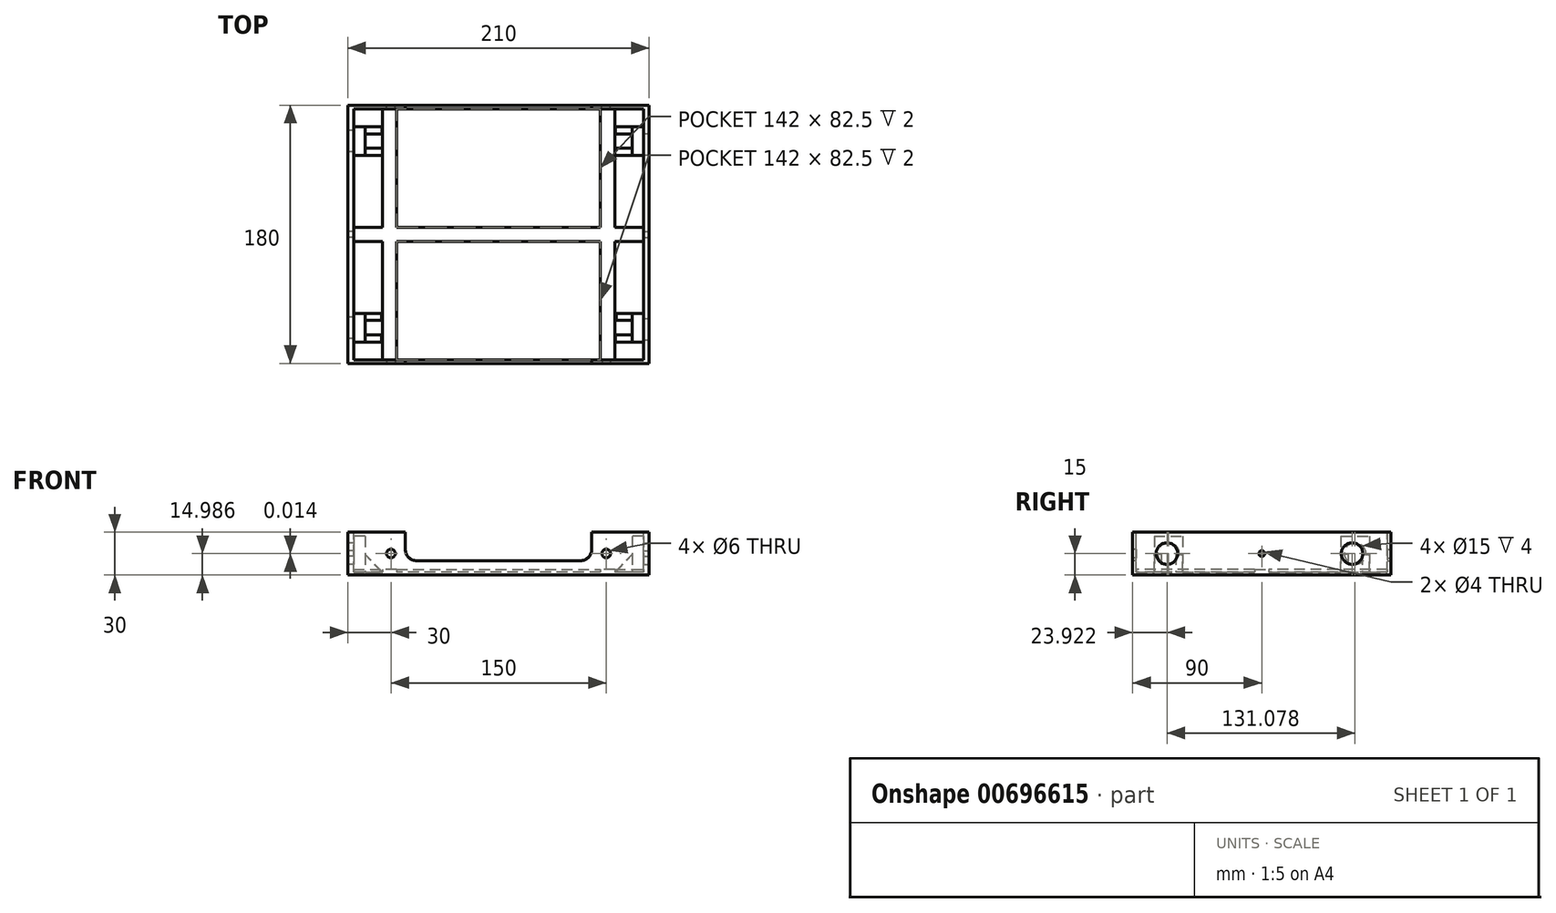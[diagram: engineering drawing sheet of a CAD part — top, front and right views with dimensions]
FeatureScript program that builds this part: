
annotation { "Feature Type Name" : "Feature", "Feature Type Description" : "" }
export const myFeature = defineFeature(function(context is Context, id is Id, definition is map)
    precondition{}
    {
        {
            var Q0;
            Q0=qCreatedBy(makeId("Top.planeOp"),FACE);
            var sketch = newSketch(context, id + "F0", { "sketchPlane" : qUnion([Q0])});
            skLineSegment(sketch, "E0.bottom", {"start": v(105, -90) * mm, "end": v(-105, -90) * mm});
            skLineSegment(sketch, "E0.top", {"start": v(105, 90) * mm, "end": v(-105, 90) * mm});
            skLineSegment(sketch, "E0.left", {"start": v(105, -90) * mm, "end": v(105, 90) * mm});
            skLineSegment(sketch, "E0.right", {"start": v(-105, -90) * mm, "end": v(-105, 90) * mm});
            skPoint(sketch, "E0.middle", {"position": v(0, 0) * mm});
            skSolve(sketch);
        }
        {
            var Q0;
            Q0=makeQuery(id+"F0.imprint","IMPRINT",FACE,{"disambiguationData":[TD([[makeQuery(id+"F0.imprint","IMPRINT",EDGE,{"derivedFrom":sQuery(id+"F0.wireOp",EDGE,"E0.bottom")}),-1.0]])]});
            extrude(context, id + "F1", {"entities" : qUnion([Q0]), "depth" : 30 * mm, "offsetDistance" : 25 * mm});
        }
        {
            var Q0;
            Q0=makeQuery(id+"F1.opExtrude","CAP_FACE",FACE,{"disambiguationData":[OSD([sQuery(id+"F0.wireOp",EDGE,"E0.bottom"),sQuery(id+"F0.wireOp",EDGE,"E0.top"),sQuery(id+"F0.wireOp",EDGE,"E0.left"),sQuery(id+"F0.wireOp",EDGE,"E0.right")])],"isStart":false});
            var sketch = newSketch(context, id + "F2", { "sketchPlane" : qUnion([Q0])});
            skLineSegment(sketch, "E1.bottom", {"start": v(101, -87.5) * mm, "end": v(-101, -87.5) * mm});
            skLineSegment(sketch, "E1.top", {"start": v(101, 87.5) * mm, "end": v(-101, 87.5) * mm});
            skLineSegment(sketch, "E1.left", {"start": v(101, -87.5) * mm, "end": v(101, 87.5) * mm});
            skLineSegment(sketch, "E1.right", {"start": v(-101, -87.5) * mm, "end": v(-101, 87.5) * mm});
            skPoint(sketch, "E1.middle", {"position": v(0, 0) * mm});
            skSolve(sketch);
        }
        {
            var Q0;
            Q0=makeQuery(id+"F2.imprint","IMPRINT",FACE,{"disambiguationData":[TD([[makeQuery(id+"F2.imprint","IMPRINT",EDGE,{"derivedFrom":sQuery(id+"F2.wireOp",EDGE,"E1.bottom")}),-1.0]])]});
            extrude(context, id + "F3", {"entities" : qUnion([Q0]), "operationType" : NewBodyOperationType.REMOVE, "oppositeDirection" : true, "depth" : 28 * mm, "offsetDistance" : 25 * mm});
        }
        {
            var Q0;
            Q0=makeQuery(id+"F1.opExtrude","SWEPT_FACE",FACE,{"disambiguationData":[OSD([sQuery(id+"F0.wireOp",EDGE,"E0.bottom")])]});
            var sketch = newSketch(context, id + "F4", { "sketchPlane" : qUnion([Q0])});
            skLineSegment(sketch, "E2", {"start": v(0, 15) * mm, "end": v(0, 30) * mm, "construction": true});
            skPoint(sketch, "E2.startSnap0", {"position": v(-105, 15) * mm});
            skPoint(sketch, "E2.startSnap1", {"position": v(0, 30) * mm});
            skLineSegment(sketch, "E3", {"start": v(0, 15) * mm, "end": v(-105, 15) * mm, "construction": true});
            skLineSegment(sketch, "E4", {"start": v(0, 15) * mm, "end": v(105, 15) * mm, "construction": true});
            skLineSegment(sketch, "E5", {"start": v(-105, 0) * mm, "end": v(-75, 0) * mm, "construction": true});
            skLineSegment(sketch, "E6", {"start": v(105, 0) * mm, "end": v(75, 0) * mm, "construction": true});
            skLineSegment(sketch, "E7", {"start": v(-75, 0) * mm, "end": v(-75, 30) * mm, "construction": true});
            skLineSegment(sketch, "E8", {"start": v(75, 0) * mm, "end": v(75, 30) * mm, "construction": true});
            skCircle(sketch, "E9", {"center": v(-75, 15) * mm, "radius": 3 * mm});
            skCircle(sketch, "E10", {"center": v(75, 15) * mm, "radius": 3 * mm});
            skLineSegment(sketch, "E11", {"start": v(-105, 30) * mm, "end": v(-65, 30) * mm, "construction": true});
            skLineSegment(sketch, "E12", {"start": v(105, 30) * mm, "end": v(73, 30) * mm, "construction": true});
            skLineSegment(sketch, "E13", {"start": v(-105, 0) * mm, "end": v(-105, 8) * mm, "construction": true});
            skLineSegment(sketch, "E14", {"start": v(-57, 10) * mm, "end": v(57, 10) * mm, "construction": true});
            skLineSegment(sketch, "E15", {"start": v(-15, 30) * mm, "end": v(-15, 0) * mm, "construction": true});
            skLineSegment(sketch, "E16", {"start": v(15, 30) * mm, "end": v(15, 0) * mm, "construction": true});
            skLineSegment(sketch, "E17", {"start": v(-15, 10) * mm, "end": v(-15, 0) * mm});
            skLineSegment(sketch, "E18", {"start": v(15, 10) * mm, "end": v(15, 0) * mm});
            skLineSegment(sketch, "E19", {"start": v(-15, 10) * mm, "end": v(15, 10) * mm});
            skLineSegment(sketch, "E20", {"start": v(-65, 30) * mm, "end": v(-65, 18) * mm, "construction": true});
            skLineSegment(sketch, "E21", {"start": v(65, 22) * mm, "end": v(65, 18) * mm, "construction": true});
            skLineSegment(sketch, "E22", {"start": v(65, 30) * mm, "end": v(65, 18) * mm});
            skLineSegment(sketch, "E23", {"start": v(57, 10) * mm, "end": v(15, 10) * mm});
            skLineSegment(sketch, "E24", {"start": v(-65, 30) * mm, "end": v(-65, 18) * mm});
            skLineSegment(sketch, "E25", {"start": v(-57, 10) * mm, "end": v(-15, 10) * mm});
            skPoint(sketch, "E26.newPointA", {"position": v(-65, 0) * mm});
            skArc(sketch, "E26.filletArc", {"start": v(-65, 18) * mm, "mid": v(-62.66, 12.34) * mm, "end": v(-57, 10) * mm, "construction": true});
            skPoint(sketch, "E27.newPointA", {"position": v(65, 0) * mm});
            skArc(sketch, "E27.filletArc", {"start": v(57, 10) * mm, "mid": v(62.66, 12.34) * mm, "end": v(65, 18) * mm, "construction": true});
            skPoint(sketch, "E28.visualSharp", {"position": v(-65, 10) * mm});
            skArc(sketch, "E28.filletArc", {"start": v(-65, 18) * mm, "mid": v(-62.66, 12.34) * mm, "end": v(-57, 10) * mm});
            skPoint(sketch, "E29.visualSharp", {"position": v(65, 10) * mm});
            skArc(sketch, "E29.filletArc", {"start": v(57, 10) * mm, "mid": v(62.66, 12.34) * mm, "end": v(65, 18) * mm});
            skPoint(sketch, "E30.visualSharp", {"position": v(65, 30) * mm});
            skArc(sketch, "E30.filletArc", {"start": v(73, 30) * mm, "mid": v(67.34, 27.66) * mm, "end": v(65, 22) * mm, "construction": true});
            skSolve(sketch);
        }
        {
            var Q0;
            Q0=makeQuery(id+"F4.imprint","IMPRINT",FACE,{"disambiguationData":[TD([[makeQuery(id+"F4.imprint","IMPRINT",EDGE,{"derivedFrom":sQuery(id+"F4.wireOp",EDGE,"E19")}),1.0]])]});
            var Q1;
            Q1=makeQuery(id+"F4.imprint","IMPRINT",FACE,{"disambiguationData":[TD([[makeQuery(id+"F4.imprint","IMPRINT",EDGE,{"derivedFrom":sQuery(id+"F4.wireOp",EDGE,"E9")}),1.0]])]});
            var Q2;
            Q2=makeQuery(id+"F4.imprint","IMPRINT",FACE,{"disambiguationData":[TD([[makeQuery(id+"F4.imprint","IMPRINT",EDGE,{"derivedFrom":sQuery(id+"F4.wireOp",EDGE,"E10")}),1.0]])]});
            extrude(context, id + "F5", {"entities" : qUnion([Q0, Q1, Q2]), "operationType" : NewBodyOperationType.REMOVE, "oppositeDirection" : true, "depth" : 4 * mm, "offsetDistance" : 25 * mm});
        }
        {
            var Q0;
            Q0=makeQuery(id+"F3.boolean.opBoolean","COPY",FACE,{"derivedFrom":makeQuery(id+"F3.opExtrude","CAP_FACE",FACE,{"disambiguationData":[OSD([sQuery(id+"F2.wireOp",EDGE,"E1.bottom"),sQuery(id+"F2.wireOp",EDGE,"E1.top"),sQuery(id+"F2.wireOp",EDGE,"E1.left"),sQuery(id+"F2.wireOp",EDGE,"E1.right")])],"isStart":false})});
            var sketch = newSketch(context, id + "F6", { "sketchPlane" : qUnion([Q0])});
            skLineSegment(sketch, "E31", {"start": v(-101, 87.5) * mm, "end": v(-81, 87.5) * mm, "construction": true});
            skLineSegment(sketch, "E32.bottom", {"start": v(-81, 87.5) * mm, "end": v(-71, 87.5) * mm});
            skLineSegment(sketch, "E32.top", {"start": v(-81, -87.5) * mm, "end": v(-71, -87.5) * mm});
            skLineSegment(sketch, "E32.left", {"start": v(-81, 87.5) * mm, "end": v(-81, -87.5) * mm});
            skLineSegment(sketch, "E32.right", {"start": v(-71, 87.5) * mm, "end": v(-71, -87.5) * mm});
            skLineSegment(sketch, "E33", {"start": v(101, 87.5) * mm, "end": v(81, 87.5) * mm, "construction": true});
            skLineSegment(sketch, "E34.bottom", {"start": v(81, 87.5) * mm, "end": v(71, 87.5) * mm});
            skLineSegment(sketch, "E34.top", {"start": v(81, -87.5) * mm, "end": v(71, -87.5) * mm});
            skLineSegment(sketch, "E34.left", {"start": v(81, 87.5) * mm, "end": v(81, -87.5) * mm});
            skLineSegment(sketch, "E34.right", {"start": v(71, 87.5) * mm, "end": v(71, -87.5) * mm});
            skLineSegment(sketch, "E35.bottom", {"start": v(-101, 5) * mm, "end": v(101, 5) * mm});
            skLineSegment(sketch, "E35.top", {"start": v(-101, -5) * mm, "end": v(101, -5) * mm});
            skLineSegment(sketch, "E35.left", {"start": v(-101, 5) * mm, "end": v(-101, -5) * mm});
            skLineSegment(sketch, "E35.right", {"start": v(101, 5) * mm, "end": v(101, -5) * mm});
            skPoint(sketch, "E35.middle", {"position": v(0, 0) * mm});
            skSolve(sketch);
        }
        {
            var Q0;
            Q0=makeQuery(id+"F6.imprint","IMPRINT",FACE,{"disambiguationData":[TD([[makeQuery(id+"F6.imprint","IMPRINT",EDGE,{"derivedFrom":sQuery(id+"F6.wireOp",EDGE,"E32.bottom")}),1.0]])]});
            var Q1;
            Q1=makeQuery(id+"F6.imprint","IMPRINT",FACE,{"disambiguationData":[TD([[makeQuery(id+"F6.imprint","IMPRINT",EDGE,{"derivedFrom":sQuery(id+"F6.wireOp",EDGE,"E34.bottom")}),1.0]])]});
            var Q2;
            {var subQ5=sQuery(id+"F6.wireOp",EDGE,"E35.left");Q2=makeQuery(id+"F6.imprint","IMPRINT",FACE,{"disambiguationData":[TD([[makeQuery(id+"F6.imprint","IMPRINT",EDGE,{"derivedFrom":subQ5}),-1.0]])]});}
            var Q3;
            {var subQ0=sQuery(id+"F6.wireOp",EDGE,"E35.bottom");var subQ1=sQuery(id+"F6.wireOp",EDGE,"E32.left");var subQ2=makeQuery(id+"F6.imprint","INTERSECT",VERTEX,{"derivedFrom":[subQ1,subQ0]});Q3=makeQuery(id+"F6.imprint","IMPRINT",FACE,{"disambiguationData":[TD([[makeQuery(id+"F6.imprint","IMPRINT",EDGE,{"disambiguationData":[TD([[subQ2,-1.0]])],"derivedFrom":subQ1}),1.0]])]});}
            var Q4;
            {var subQ0=sQuery(id+"F6.wireOp",EDGE,"E32.top");Q4=makeQuery(id+"F6.imprint","IMPRINT",FACE,{"disambiguationData":[TD([[makeQuery(id+"F6.imprint","IMPRINT",EDGE,{"derivedFrom":subQ0}),-1.0]])]});}
            var Q5;
            {var subQ0=sQuery(id+"F6.wireOp",EDGE,"E35.bottom");var subQ1=sQuery(id+"F6.wireOp",EDGE,"E32.right");var subQ2=makeQuery(id+"F6.imprint","INTERSECT",VERTEX,{"derivedFrom":[subQ1,subQ0]});Q5=makeQuery(id+"F6.imprint","IMPRINT",FACE,{"disambiguationData":[TD([[makeQuery(id+"F6.imprint","IMPRINT",EDGE,{"disambiguationData":[TD([[subQ2,-1.0]])],"derivedFrom":subQ1}),1.0]])]});}
            var Q6;
            {var subQ0=sQuery(id+"F6.wireOp",EDGE,"E35.bottom");var subQ1=sQuery(id+"F6.wireOp",EDGE,"E34.left");var subQ2=makeQuery(id+"F6.imprint","INTERSECT",VERTEX,{"derivedFrom":[subQ1,subQ0]});Q6=makeQuery(id+"F6.imprint","IMPRINT",FACE,{"disambiguationData":[TD([[makeQuery(id+"F6.imprint","IMPRINT",EDGE,{"disambiguationData":[TD([[subQ2,-1.0]])],"derivedFrom":subQ1}),-1.0]])]});}
            var Q7;
            {var subQ0=sQuery(id+"F6.wireOp",EDGE,"E34.top");Q7=makeQuery(id+"F6.imprint","IMPRINT",FACE,{"disambiguationData":[TD([[makeQuery(id+"F6.imprint","IMPRINT",EDGE,{"derivedFrom":subQ0}),-1.0]])]});}
            var Q8;
            {var subQ5=sQuery(id+"F6.wireOp",EDGE,"E35.right");Q8=makeQuery(id+"F6.imprint","IMPRINT",FACE,{"disambiguationData":[TD([[makeQuery(id+"F6.imprint","IMPRINT",EDGE,{"derivedFrom":subQ5}),1.0]])]});}
            extrude(context, id + "F7", {"entities" : qUnion([Q0, Q1, Q2, Q3, Q4, Q5, Q6, Q7, Q8]), "depth" : 2 * mm, "offsetDistance" : 25 * mm});
        }
        {
            var Q0;
            Q0=makeQuery(id+"F1.opExtrude","SWEPT_FACE",FACE,{"disambiguationData":[OSD([sQuery(id+"F0.wireOp",EDGE,"E0.left")])]});
            var sketch = newSketch(context, id + "F8", { "sketchPlane" : qUnion([Q0])});
            skLineSegment(sketch, "E36", {"start": v(0, 30) * mm, "end": v(0, 0) * mm, "construction": true});
            skLineSegment(sketch, "E37", {"start": v(-90, 15) * mm, "end": v(90, 15) * mm, "construction": true});
            skCircle(sketch, "E38", {"center": v(0, 15) * mm, "radius": 2 * mm});
            skSolve(sketch);
        }
        {
            var Q0;
            Q0=makeQuery(id+"F8.imprint","IMPRINT",FACE,{"disambiguationData":[TD([[makeQuery(id+"F8.imprint","IMPRINT",EDGE,{"derivedFrom":sQuery(id+"F8.wireOp",EDGE,"E38")}),1.0]])]});
            var Q1;
            Q1=makeQuery(id+"F8.imprint","IMPRINT",FACE,{"disambiguationData":[TD([[makeQuery(id+"F8.imprint","IMPRINT",EDGE,{"derivedFrom":sQuery(id+"F8.wireOp",EDGE,"LcwHPbP9-Mx9n-9gbT-e416-QBVYges8Fovk")}),1.0]])]});
            extrude(context, id + "F9", {"entities" : qUnion([Q0, Q1]), "operationType" : NewBodyOperationType.REMOVE, "oppositeDirection" : true, "depth" : 5 * mm, "offsetDistance" : 25 * mm});
        }
        {
            var Q0;
            Q0=makeQuery(id+"F1.opExtrude","SWEPT_FACE",FACE,{"disambiguationData":[OSD([sQuery(id+"F0.wireOp",EDGE,"E0.right")])]});
            var sketch = newSketch(context, id + "F10", { "sketchPlane" : qUnion([Q0])});
            skLineSegment(sketch, "E39", {"start": v(0, 30) * mm, "end": v(0, 0) * mm, "construction": true});
            skLineSegment(sketch, "E40", {"start": v(-90, 15) * mm, "end": v(90, 15) * mm, "construction": true});
            skCircle(sketch, "E41", {"center": v(0, 15) * mm, "radius": 2 * mm});
            skLineSegment(sketch, "E42", {"start": v(-65, 30) * mm, "end": v(-65, 0) * mm, "construction": true});
            skLineSegment(sketch, "E43", {"start": v(65, 30) * mm, "end": v(65, 0) * mm, "construction": true});
            skCircle(sketch, "E44", {"center": v(-65, 15) * mm, "radius": 7.5 * mm});
            skCircle(sketch, "E45", {"center": v(65, 15) * mm, "radius": 7.5 * mm});
            skSolve(sketch);
        }
        {
            var Q0;
            Q0=makeQuery(id+"F10.imprint","IMPRINT",FACE,{"disambiguationData":[TD([[makeQuery(id+"F10.imprint","IMPRINT",EDGE,{"derivedFrom":sQuery(id+"F10.wireOp",EDGE,"E41")}),1.0]])]});
            var Q1;
            Q1=makeQuery(id+"F10.imprint","IMPRINT",FACE,{"disambiguationData":[TD([[makeQuery(id+"F10.imprint","IMPRINT",EDGE,{"derivedFrom":sQuery(id+"F10.wireOp",EDGE,"E44")}),1.0]])]});
            var Q2;
            Q2=makeQuery(id+"F10.imprint","IMPRINT",FACE,{"disambiguationData":[TD([[makeQuery(id+"F10.imprint","IMPRINT",EDGE,{"derivedFrom":sQuery(id+"F10.wireOp",EDGE,"E45")}),1.0]])]});
            extrude(context, id + "F11", {"entities" : qUnion([Q0, Q1, Q2]), "operationType" : NewBodyOperationType.REMOVE, "oppositeDirection" : true, "depth" : 5 * mm, "offsetDistance" : 25 * mm});
        }
        {
            var Q0;
            Q0=makeQuery(id+"F1.opExtrude","SWEPT_FACE",FACE,{"disambiguationData":[OSD([sQuery(id+"F0.wireOp",EDGE,"E0.left")])]});
            var sketch = newSketch(context, id + "F12", { "sketchPlane" : qUnion([Q0])});
            skLineSegment(sketch, "E46", {"start": v(-66.08, 30) * mm, "end": v(-66.08, 0) * mm, "construction": true});
            skLineSegment(sketch, "E47", {"start": v(62.94, 30) * mm, "end": v(62.94, 0) * mm, "construction": true});
            skLineSegment(sketch, "E48", {"start": v(-90, 15) * mm, "end": v(90, 15) * mm, "construction": true});
            skCircle(sketch, "E49", {"center": v(-66.08, 15) * mm, "radius": 7.5 * mm});
            skCircle(sketch, "E50", {"center": v(62.94, 15) * mm, "radius": 7.5 * mm});
            skSolve(sketch);
        }
        {
            var Q0;
            Q0=makeQuery(id+"F12.imprint","IMPRINT",FACE,{"disambiguationData":[TD([[makeQuery(id+"F12.imprint","IMPRINT",EDGE,{"derivedFrom":sQuery(id+"F12.wireOp",EDGE,"E49")}),1.0]])]});
            var Q1;
            Q1=makeQuery(id+"F12.imprint","IMPRINT",FACE,{"disambiguationData":[TD([[makeQuery(id+"F12.imprint","IMPRINT",EDGE,{"derivedFrom":sQuery(id+"F12.wireOp",EDGE,"E50")}),1.0]])]});
            extrude(context, id + "F13", {"entities" : qUnion([Q0, Q1]), "operationType" : NewBodyOperationType.REMOVE, "oppositeDirection" : true, "depth" : 5 * mm, "offsetDistance" : 25 * mm});
        }
        {
            var Q0;
            Q0=makeQuery(id+"F3.boolean.opBoolean","COPY",FACE,{"derivedFrom":makeQuery(id+"F3.opExtrude","CAP_FACE",FACE,{"disambiguationData":[OSD([sQuery(id+"F2.wireOp",EDGE,"E1.bottom"),sQuery(id+"F2.wireOp",EDGE,"E1.top"),sQuery(id+"F2.wireOp",EDGE,"E1.left"),sQuery(id+"F2.wireOp",EDGE,"E1.right")])],"isStart":false})});
            var sketch = newSketch(context, id + "F14", { "sketchPlane" : qUnion([Q0])});
            skLineSegment(sketch, "E51", {"start": v(-101, 65) * mm, "end": v(101, 65) * mm, "construction": true});
            skLineSegment(sketch, "E52", {"start": v(-101, -65) * mm, "end": v(101, -65) * mm, "construction": true});
            skLineSegment(sketch, "E53", {"start": v(-97, 87.5) * mm, "end": v(-97, -87.5) * mm, "construction": true});
            skLineSegment(sketch, "E54", {"start": v(97, 87.5) * mm, "end": v(97, -87.5) * mm, "construction": true});
            skPoint(sketch, "E55.middle", {"position": v(-97, -65) * mm});
            skLineSegment(sketch, "E56.bottom", {"start": v(-93, -75) * mm, "end": v(-101, -75) * mm});
            skLineSegment(sketch, "E56.top", {"start": v(-93, -55) * mm, "end": v(-101, -55) * mm});
            skLineSegment(sketch, "E56.left", {"start": v(-93, -75) * mm, "end": v(-93, -55) * mm});
            skLineSegment(sketch, "E56.right", {"start": v(-101, -75) * mm, "end": v(-101, -55) * mm});
            skLineSegment(sketch, "E57.bottom", {"start": v(-93, 55) * mm, "end": v(-101, 55) * mm});
            skLineSegment(sketch, "E57.top", {"start": v(-93, 75) * mm, "end": v(-101, 75) * mm});
            skLineSegment(sketch, "E57.left", {"start": v(-93, 55) * mm, "end": v(-93, 75) * mm});
            skLineSegment(sketch, "E57.right", {"start": v(-101, 55) * mm, "end": v(-101, 75) * mm});
            skPoint(sketch, "E57.middle", {"position": v(-97, 65) * mm});
            skLineSegment(sketch, "E58.bottom", {"start": v(101, 55) * mm, "end": v(93, 55) * mm});
            skLineSegment(sketch, "E58.top", {"start": v(101, 75) * mm, "end": v(93, 75) * mm});
            skLineSegment(sketch, "E58.left", {"start": v(101, 55) * mm, "end": v(101, 75) * mm});
            skLineSegment(sketch, "E58.right", {"start": v(93, 55) * mm, "end": v(93, 75) * mm});
            skPoint(sketch, "E58.middle", {"position": v(97, 65) * mm});
            skLineSegment(sketch, "E59.bottom", {"start": v(101, -75) * mm, "end": v(93, -75) * mm});
            skLineSegment(sketch, "E59.top", {"start": v(101, -55) * mm, "end": v(93, -55) * mm});
            skLineSegment(sketch, "E59.left", {"start": v(101, -75) * mm, "end": v(101, -55) * mm});
            skLineSegment(sketch, "E59.right", {"start": v(93, -75) * mm, "end": v(93, -55) * mm});
            skPoint(sketch, "E59.middle", {"position": v(97, -65) * mm});
            skSolve(sketch);
        }
        {
            var Q0;
            Q0=makeQuery(id+"F14.imprint","IMPRINT",FACE,{"disambiguationData":[TD([[makeQuery(id+"F14.imprint","IMPRINT",EDGE,{"derivedFrom":sQuery(id+"F14.wireOp",EDGE,"E57.bottom")}),-1.0]])]});
            var Q1;
            Q1=makeQuery(id+"F14.imprint","IMPRINT",FACE,{"disambiguationData":[TD([[makeQuery(id+"F14.imprint","IMPRINT",EDGE,{"derivedFrom":sQuery(id+"F14.wireOp",EDGE,"E56.bottom")}),-1.0]])]});
            var Q2;
            Q2=makeQuery(id+"F14.imprint","IMPRINT",FACE,{"disambiguationData":[TD([[makeQuery(id+"F14.imprint","IMPRINT",EDGE,{"derivedFrom":sQuery(id+"F14.wireOp",EDGE,"E58.bottom")}),-1.0]])]});
            var Q3;
            Q3=makeQuery(id+"F14.imprint","IMPRINT",FACE,{"disambiguationData":[TD([[makeQuery(id+"F14.imprint","IMPRINT",EDGE,{"derivedFrom":sQuery(id+"F14.wireOp",EDGE,"E59.bottom")}),-1.0]])]});
            extrude(context, id + "F15", {"entities" : qUnion([Q0, Q1, Q2, Q3]), "operationType" : NewBodyOperationType.ADD, "depth" : 25 * mm, "offsetDistance" : 25 * mm});
        }
        {
            var Q0;
            Q0=makeQuery(id+"F15.opExtrude","SWEPT_FACE",FACE,{"disambiguationData":[OSD([sQuery(id+"F14.wireOp",EDGE,"E59.top")])]});
            var sketch = newSketch(context, id + "F16", { "sketchPlane" : qUnion([Q0])});
            skLineSegment(sketch, "E60", {"start": v(-81.63, 1.7) * mm, "end": v(-93, 2) * mm});
            skLineSegment(sketch, "E61", {"start": v(-81.63, 1.7) * mm, "end": v(-93, 14.5) * mm});
            skSolve(sketch);
        }
        {
            var Q0;
            {var subQ0=sQuery(id+"F16.wireOp",EDGE,"E60");Q0=makeQuery(id+"F16.imprint","IMPRINT",FACE,{"disambiguationData":[TD([[makeQuery(id+"F16.imprint","IMPRINT",EDGE,{"derivedFrom":subQ0}),-1.0]])]});}
            extrude(context, id + "F17", {"entities" : qUnion([Q0]), "operationType" : NewBodyOperationType.ADD, "oppositeDirection" : true, "depth" : 5 * mm, "offsetDistance" : 25 * mm});
        }
        {
            var Q0;
            Q0=makeQuery(id+"F15.opExtrude","SWEPT_FACE",FACE,{"disambiguationData":[OSD([sQuery(id+"F14.wireOp",EDGE,"E57.bottom")])]});
            var sketch = newSketch(context, id + "F18", { "sketchPlane" : qUnion([Q0])});
            skLineSegment(sketch, "E62", {"start": v(-93, 2) * mm, "end": v(-81.02, 2) * mm});
            skLineSegment(sketch, "E63", {"start": v(-81.02, 2) * mm, "end": v(-93, 14.5) * mm});
            skSolve(sketch);
        }
        {
            var Q0;
            {var subQ0=sQuery(id+"F18.wireOp",EDGE,"3tv4UPtd-VhHN-JNsJ-59JR-FFOhHBoCQ9kc");Q0=makeQuery(id+"F18.imprint","IMPRINT",FACE,{"disambiguationData":[TD([[makeQuery(id+"F18.imprint","IMPRINT",EDGE,{"derivedFrom":subQ0}),1.0]])]});}
            var Q1;
            {var subQ0=sQuery(id+"F18.wireOp",EDGE,"E62");Q1=makeQuery(id+"F18.imprint","IMPRINT",FACE,{"disambiguationData":[TD([[makeQuery(id+"F18.imprint","IMPRINT",EDGE,{"derivedFrom":subQ0}),1.0]])]});}
            extrude(context, id + "F19", {"entities" : qUnion([Q0, Q1]), "operationType" : NewBodyOperationType.ADD, "oppositeDirection" : true, "depth" : 5 * mm, "offsetDistance" : 25 * mm});
        }
        {
            var Q0;
            Q0=makeQuery(id+"F15.opExtrude","SWEPT_FACE",FACE,{"disambiguationData":[OSD([sQuery(id+"F14.wireOp",EDGE,"E58.bottom")])]});
            var sketch = newSketch(context, id + "F20", { "sketchPlane" : qUnion([Q0])});
            skLineSegment(sketch, "E64", {"start": v(93, 2) * mm, "end": v(81.16, 2) * mm});
            skLineSegment(sketch, "E65", {"start": v(81.16, 2) * mm, "end": v(93, 14.5) * mm});
            skSolve(sketch);
        }
        {
            var Q0;
            {var subQ0=sQuery(id+"F20.wireOp",EDGE,"E64");Q0=makeQuery(id+"F20.imprint","IMPRINT",FACE,{"disambiguationData":[TD([[makeQuery(id+"F20.imprint","IMPRINT",EDGE,{"derivedFrom":subQ0}),-1.0]])]});}
            extrude(context, id + "F21", {"entities" : qUnion([Q0]), "operationType" : NewBodyOperationType.ADD, "oppositeDirection" : true, "depth" : 5 * mm, "offsetDistance" : 25 * mm});
        }
        {
            var Q0;
            Q0=makeQuery(id+"F15.opExtrude","SWEPT_FACE",FACE,{"disambiguationData":[OSD([sQuery(id+"F14.wireOp",EDGE,"E56.top")])]});
            var sketch = newSketch(context, id + "F22", { "sketchPlane" : qUnion([Q0])});
            skLineSegment(sketch, "E66", {"start": v(93, 2) * mm, "end": v(81.4, 2) * mm});
            skLineSegment(sketch, "E67", {"start": v(81.4, 2) * mm, "end": v(93, 14.5) * mm});
            skSolve(sketch);
        }
        {
            var Q0;
            {var subQ0=sQuery(id+"F22.wireOp",EDGE,"E66");Q0=makeQuery(id+"F22.imprint","IMPRINT",FACE,{"disambiguationData":[TD([[makeQuery(id+"F22.imprint","IMPRINT",EDGE,{"derivedFrom":subQ0}),-1.0]])]});}
            extrude(context, id + "F23", {"entities" : qUnion([Q0]), "operationType" : NewBodyOperationType.ADD, "oppositeDirection" : true, "depth" : 5 * mm, "offsetDistance" : 25 * mm});
        }
        {
            var Q0;
            Q0=makeQuery(id+"F15.opExtrude","SWEPT_FACE",FACE,{"disambiguationData":[OSD([sQuery(id+"F14.wireOp",EDGE,"E57.top")])]});
            var sketch = newSketch(context, id + "F24", { "sketchPlane" : qUnion([Q0])});
            skLineSegment(sketch, "E68", {"start": v(93, 2) * mm, "end": v(81.21, 2) * mm});
            skLineSegment(sketch, "E69", {"start": v(81.21, 2) * mm, "end": v(93, 14.5) * mm});
            skSolve(sketch);
        }
        {
            var Q0;
            {var subQ0=sQuery(id+"F24.wireOp",EDGE,"E68");Q0=makeQuery(id+"F24.imprint","IMPRINT",FACE,{"disambiguationData":[TD([[makeQuery(id+"F24.imprint","IMPRINT",EDGE,{"derivedFrom":subQ0}),-1.0]])]});}
            extrude(context, id + "F25", {"entities" : qUnion([Q0]), "operationType" : NewBodyOperationType.ADD, "oppositeDirection" : true, "depth" : 5 * mm, "offsetDistance" : 25 * mm});
        }
        {
            var Q0;
            Q0=makeQuery(id+"F15.opExtrude","SWEPT_FACE",FACE,{"disambiguationData":[OSD([sQuery(id+"F14.wireOp",EDGE,"E59.bottom")])]});
            var sketch = newSketch(context, id + "F26", { "sketchPlane" : qUnion([Q0])});
            skLineSegment(sketch, "E70", {"start": v(93, 2) * mm, "end": v(81.3, 2) * mm});
            skLineSegment(sketch, "E71", {"start": v(81.3, 2) * mm, "end": v(93, 14.5) * mm});
            skSolve(sketch);
        }
        {
            var Q0;
            {var subQ0=sQuery(id+"F26.wireOp",EDGE,"E70");Q0=makeQuery(id+"F26.imprint","IMPRINT",FACE,{"disambiguationData":[TD([[makeQuery(id+"F26.imprint","IMPRINT",EDGE,{"derivedFrom":subQ0}),-1.0]])]});}
            extrude(context, id + "F27", {"entities" : qUnion([Q0]), "operationType" : NewBodyOperationType.ADD, "oppositeDirection" : true, "depth" : 5 * mm, "offsetDistance" : 25 * mm});
        }
        {
            var Q0;
            Q0=makeQuery(id+"F1.opExtrude","SWEPT_BODY",BODY,{"disambiguationData":[OSD([sQuery(id+"F0.wireOp",EDGE,"E0.bottom"),sQuery(id+"F0.wireOp",EDGE,"E0.top"),sQuery(id+"F0.wireOp",EDGE,"E0.left"),sQuery(id+"F0.wireOp",EDGE,"E0.right")])]});
            var Q1;
            Q1=makeQuery(id+"F7.opExtrude","SWEPT_BODY",BODY,{"disambiguationData":[OSD([sQuery(id+"F6.wireOp",EDGE,"E32.bottom"),sQuery(id+"F6.wireOp",EDGE,"E32.top"),sQuery(id+"F6.wireOp",EDGE,"E32.left"),sQuery(id+"F6.wireOp",EDGE,"E32.right"),sQuery(id+"F6.wireOp",EDGE,"E34.bottom"),sQuery(id+"F6.wireOp",EDGE,"E34.top"),sQuery(id+"F6.wireOp",EDGE,"E34.left"),sQuery(id+"F6.wireOp",EDGE,"E34.right"),sQuery(id+"F6.wireOp",EDGE,"E35.bottom"),sQuery(id+"F6.wireOp",EDGE,"E35.top"),sQuery(id+"F6.wireOp",EDGE,"E35.left"),sQuery(id+"F6.wireOp",EDGE,"E35.right")])]});
            booleanBodies(context, id + "F28", {"operationType" : BooleanOperationType.UNION, "tools" : qUnion([Q0, Q1])});
        }
        {
            var Q0;
            Q0=makeQuery(id+"F15.opExtrude","SWEPT_FACE",FACE,{"disambiguationData":[OSD([sQuery(id+"F14.wireOp",EDGE,"E56.bottom")])]});
            var sketch = newSketch(context, id + "F29", { "sketchPlane" : qUnion([Q0])});
            skLineSegment(sketch, "E72", {"start": v(-93, 2) * mm, "end": v(-81.42, 2) * mm});
            skLineSegment(sketch, "E73", {"start": v(-81.42, 2) * mm, "end": v(-93, 14.5) * mm});
            skSolve(sketch);
        }
        {
            var Q0;
            {var subQ0=sQuery(id+"F29.wireOp",EDGE,"E72");Q0=makeQuery(id+"F29.imprint","IMPRINT",FACE,{"disambiguationData":[TD([[makeQuery(id+"F29.imprint","IMPRINT",EDGE,{"derivedFrom":subQ0}),1.0]])]});}
            extrude(context, id + "F30", {"entities" : qUnion([Q0]), "operationType" : NewBodyOperationType.ADD, "oppositeDirection" : true, "depth" : 5 * mm, "offsetDistance" : 25 * mm});
        }
        {
            var Q0;
            Q0=makeQuery(id+"F15.opExtrude","SWEPT_FACE",FACE,{"disambiguationData":[OSD([sQuery(id+"F14.wireOp",EDGE,"E58.top")])]});
            var sketch = newSketch(context, id + "F31", { "sketchPlane" : qUnion([Q0])});
            skLineSegment(sketch, "E74", {"start": v(-93, 2) * mm, "end": v(-81.28, 2) * mm});
            skLineSegment(sketch, "E75", {"start": v(-81.28, 2) * mm, "end": v(-93, 14.5) * mm});
            skSolve(sketch);
        }
        {
            var Q0;
            {var subQ0=sQuery(id+"F31.wireOp",EDGE,"E74");Q0=makeQuery(id+"F31.imprint","IMPRINT",FACE,{"disambiguationData":[TD([[makeQuery(id+"F31.imprint","IMPRINT",EDGE,{"derivedFrom":subQ0}),1.0]])]});}
            extrude(context, id + "F32", {"entities" : qUnion([Q0]), "operationType" : NewBodyOperationType.ADD, "oppositeDirection" : true, "depth" : 5 * mm, "offsetDistance" : 25 * mm});
        }
        {
            var Q0;
            Q0=makeQuery(id+"F1.opExtrude","SWEPT_FACE",FACE,{"disambiguationData":[OSD([sQuery(id+"F0.wireOp",EDGE,"E0.top")])]});
            var sketch = newSketch(context, id + "F33", { "sketchPlane" : qUnion([Q0])});
            skLineSegment(sketch, "E76", {"start": v(0, 0) * mm, "end": v(0, 30) * mm, "construction": true});
            skPoint(sketch, "E76.startSnap0", {"position": v(-105, 0) * mm});
            skPoint(sketch, "E76.startSnap1", {"position": v(0, 30) * mm});
            skLineSegment(sketch, "E77", {"start": v(0, 0) * mm, "end": v(-105, 0) * mm, "construction": true});
            skLineSegment(sketch, "E78", {"start": v(0, 0) * mm, "end": v(105, 0) * mm, "construction": true});
            skLineSegment(sketch, "E79", {"start": v(-105, 0) * mm, "end": v(-75, -0.03) * mm, "construction": true});
            skLineSegment(sketch, "E80", {"start": v(105, 0) * mm, "end": v(75, 0) * mm, "construction": true});
            skLineSegment(sketch, "E81", {"start": v(-75, -0.03) * mm, "end": v(-74.97, 30) * mm, "construction": true});
            skLineSegment(sketch, "E82", {"start": v(75, 0) * mm, "end": v(75, 30) * mm, "construction": true});
            skCircle(sketch, "E83", {"center": v(-74.99, 14.99) * mm, "radius": 3 * mm});
            skCircle(sketch, "E84", {"center": v(75, 15) * mm, "radius": 3 * mm});
            skLineSegment(sketch, "E85", {"start": v(-105, 30) * mm, "end": v(-65, 30) * mm, "construction": true});
            skLineSegment(sketch, "E86", {"start": v(105, 30) * mm, "end": v(73, 30) * mm, "construction": true});
            skLineSegment(sketch, "E87", {"start": v(-105, 0) * mm, "end": v(-105, 10) * mm, "construction": true});
            skLineSegment(sketch, "E88", {"start": v(-57, 10.06) * mm, "end": v(57, 10.06) * mm, "construction": true});
            skLineSegment(sketch, "E89", {"start": v(-15, 30) * mm, "end": v(-15, 0) * mm, "construction": true});
            skLineSegment(sketch, "E90", {"start": v(15, 0) * mm, "end": v(15, 30) * mm, "construction": true});
            skLineSegment(sketch, "E91", {"start": v(-15, 10.06) * mm, "end": v(-15, 0) * mm});
            skLineSegment(sketch, "E92", {"start": v(15, 0) * mm, "end": v(15, 10.06) * mm});
            skLineSegment(sketch, "E93", {"start": v(-15, 10.06) * mm, "end": v(15, 10.06) * mm});
            skLineSegment(sketch, "E94", {"start": v(-65, 30) * mm, "end": v(-65, 18.06) * mm, "construction": true});
            skLineSegment(sketch, "E95", {"start": v(65, 22) * mm, "end": v(65, 18.06) * mm, "construction": true});
            skLineSegment(sketch, "E96", {"start": v(65, 30) * mm, "end": v(65, 18.06) * mm});
            skLineSegment(sketch, "E97", {"start": v(57, 10.06) * mm, "end": v(15, 10.06) * mm});
            skLineSegment(sketch, "E98", {"start": v(-65, 30) * mm, "end": v(-65, 18.06) * mm});
            skLineSegment(sketch, "E99", {"start": v(-57, 10.06) * mm, "end": v(-15, 10.06) * mm});
            skPoint(sketch, "E100.newPointA", {"position": v(-65, 0) * mm});
            skArc(sketch, "E100.filletArc", {"start": v(-65, 18.06) * mm, "mid": v(-62.66, 12.4) * mm, "end": v(-57, 10.06) * mm, "construction": true});
            skPoint(sketch, "E101.newPointA", {"position": v(65, -0.04) * mm});
            skArc(sketch, "E101.filletArc", {"start": v(57, 10.06) * mm, "mid": v(62.66, 12.4) * mm, "end": v(65, 18.06) * mm, "construction": true});
            skPoint(sketch, "E102.visualSharp", {"position": v(-65, 10.06) * mm});
            skArc(sketch, "E102.filletArc", {"start": v(-65, 18.06) * mm, "mid": v(-62.66, 12.4) * mm, "end": v(-57, 10.06) * mm});
            skPoint(sketch, "E103.visualSharp", {"position": v(65, 10.06) * mm});
            skArc(sketch, "E103.filletArc", {"start": v(57, 10.06) * mm, "mid": v(62.66, 12.4) * mm, "end": v(65, 18.06) * mm});
            skPoint(sketch, "E104.visualSharp", {"position": v(65, 30) * mm});
            skArc(sketch, "E104.filletArc", {"start": v(73, 30) * mm, "mid": v(67.34, 27.66) * mm, "end": v(65, 22) * mm, "construction": true});
            skLineSegment(sketch, "E105", {"start": v(-105, 15) * mm, "end": v(105, 15) * mm, "construction": true});
            skSolve(sketch);
        }
        {
            var Q0;
            Q0=makeQuery(id+"F33.imprint","IMPRINT",FACE,{"disambiguationData":[TD([[makeQuery(id+"F33.imprint","IMPRINT",EDGE,{"derivedFrom":sQuery(id+"F33.wireOp",EDGE,"E93")}),1.0]])]});
            var Q1;
            Q1=makeQuery(id+"F33.imprint","IMPRINT",FACE,{"disambiguationData":[TD([[makeQuery(id+"F33.imprint","IMPRINT",EDGE,{"derivedFrom":sQuery(id+"F33.wireOp",EDGE,"E83")}),1.0]])]});
            var Q2;
            Q2=makeQuery(id+"F33.imprint","IMPRINT",FACE,{"disambiguationData":[TD([[makeQuery(id+"F33.imprint","IMPRINT",EDGE,{"derivedFrom":sQuery(id+"F33.wireOp",EDGE,"E84")}),1.0]])]});
            extrude(context, id + "F34", {"entities" : qUnion([Q0, Q1, Q2]), "operationType" : NewBodyOperationType.REMOVE, "oppositeDirection" : true, "depth" : 4 * mm, "offsetDistance" : 25 * mm});
        }
    });
